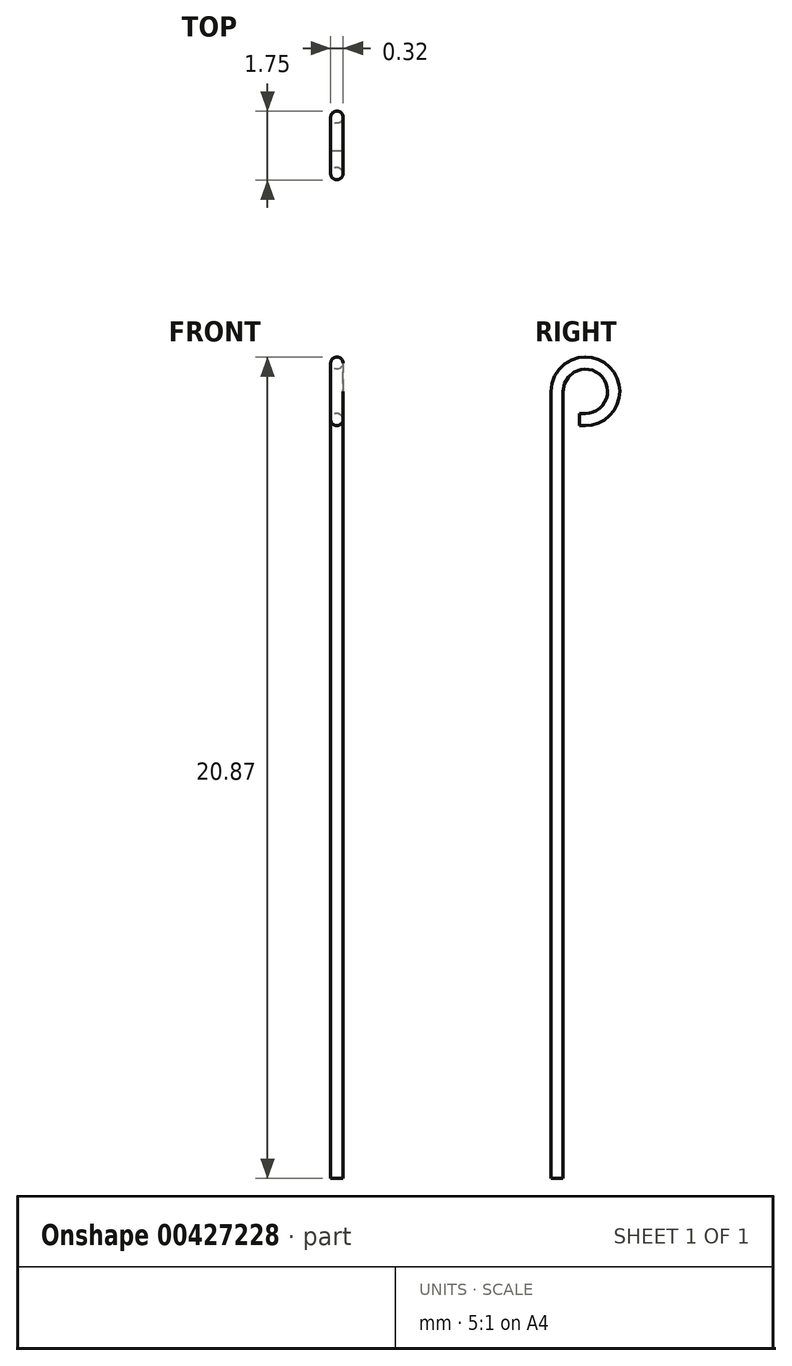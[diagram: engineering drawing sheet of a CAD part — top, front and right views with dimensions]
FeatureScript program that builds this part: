
annotation { "Feature Type Name" : "Feature", "Feature Type Description" : "" }
export const myFeature = defineFeature(function(context is Context, id is Id, definition is map)
    precondition{}
    {
        {
            var Q0;
            Q0=qCreatedBy(makeId("Top.planeOp"),FACE);
            var sketch = newSketch(context, id + "F0", { "sketchPlane" : qUnion([Q0])});
            skCircle(sketch, "E0", {"center": v(0, 0) * mm, "radius": 0.16 * mm});
            skSolve(sketch);
        }
        {
            var Q0;
            Q0 = qSketchRegion(id + "F0", true);
            extrude(context, id + "F1", {"entities" : qUnion([Q0]), "depth" : 20 * mm});
        }
        {
            var Q0;
            Q0=makeQuery(id+"F1.opExtrude","CAP_FACE",FACE,{"disambiguationData":[OSD([sQuery(id+"F0.wireOp",EDGE,"E0")])],"isStart":false});
            var sketch = newSketch(context, id + "F2", { "sketchPlane" : qUnion([Q0])});
            skCircle(sketch, "E1", {"center": v(0, 0) * mm, "radius": 0.15 * mm});
            skLineSegment(sketch, "E2", {"start": v(-2.46, 0.72) * mm, "end": v(2.55, 0.72) * mm});
            skSolve(sketch);
        }
        {
            var Q0;
            Q0=makeQuery(id+"F2.imprint","IMPRINT",FACE,{"disambiguationData":[TD([[makeQuery(id+"F2.imprint","IMPRINT",EDGE,{"derivedFrom":sQuery(id+"F2.wireOp",EDGE,"E1")}),1.0]])]});
            var Q1;
            Q1=sQuery(id+"F2.wireOp",EDGE,"E2");
            revolve(context, id + "F3", {"operationType" : NewBodyOperationType.ADD, "entities" : qUnion([Q0]), "axis" : qUnion([Q1]), "revolveType" : RevolveType.ONE_DIRECTION, "oppositeDirection" : true, "angle" : 270 * degree});
        }
        {
            var Q0;
            Q0=makeQuery(id+"F3.opRevolve","CAP_FACE",FACE,{"disambiguationData":[OSD([sQuery(id+"F2.wireOp",EDGE,"E1")])],"isStart":false});
            var sketch = newSketch(context, id + "F4", { "sketchPlane" : qUnion([Q0])});
            skSolve(sketch);
        }
        {
            var Q0;
            Q0=makeQuery(id+"F4.imprint","IMPRINT",FACE,{"disambiguationData":[TD([[makeQuery(id+"F4.imprint","IMPRINT",EDGE,{"derivedFrom":makeQuery(id+"F3.opRevolve","CAP_EDGE",EDGE,{"disambiguationData":[OSD([sQuery(id+"F2.wireOp",EDGE,"E1")])],"isStart":false})}),1.0]])]});
            extrude(context, id + "F5", {"entities" : qUnion([Q0]), "operationType" : NewBodyOperationType.ADD, "depth" : 0.15 * mm});
        }
    });
